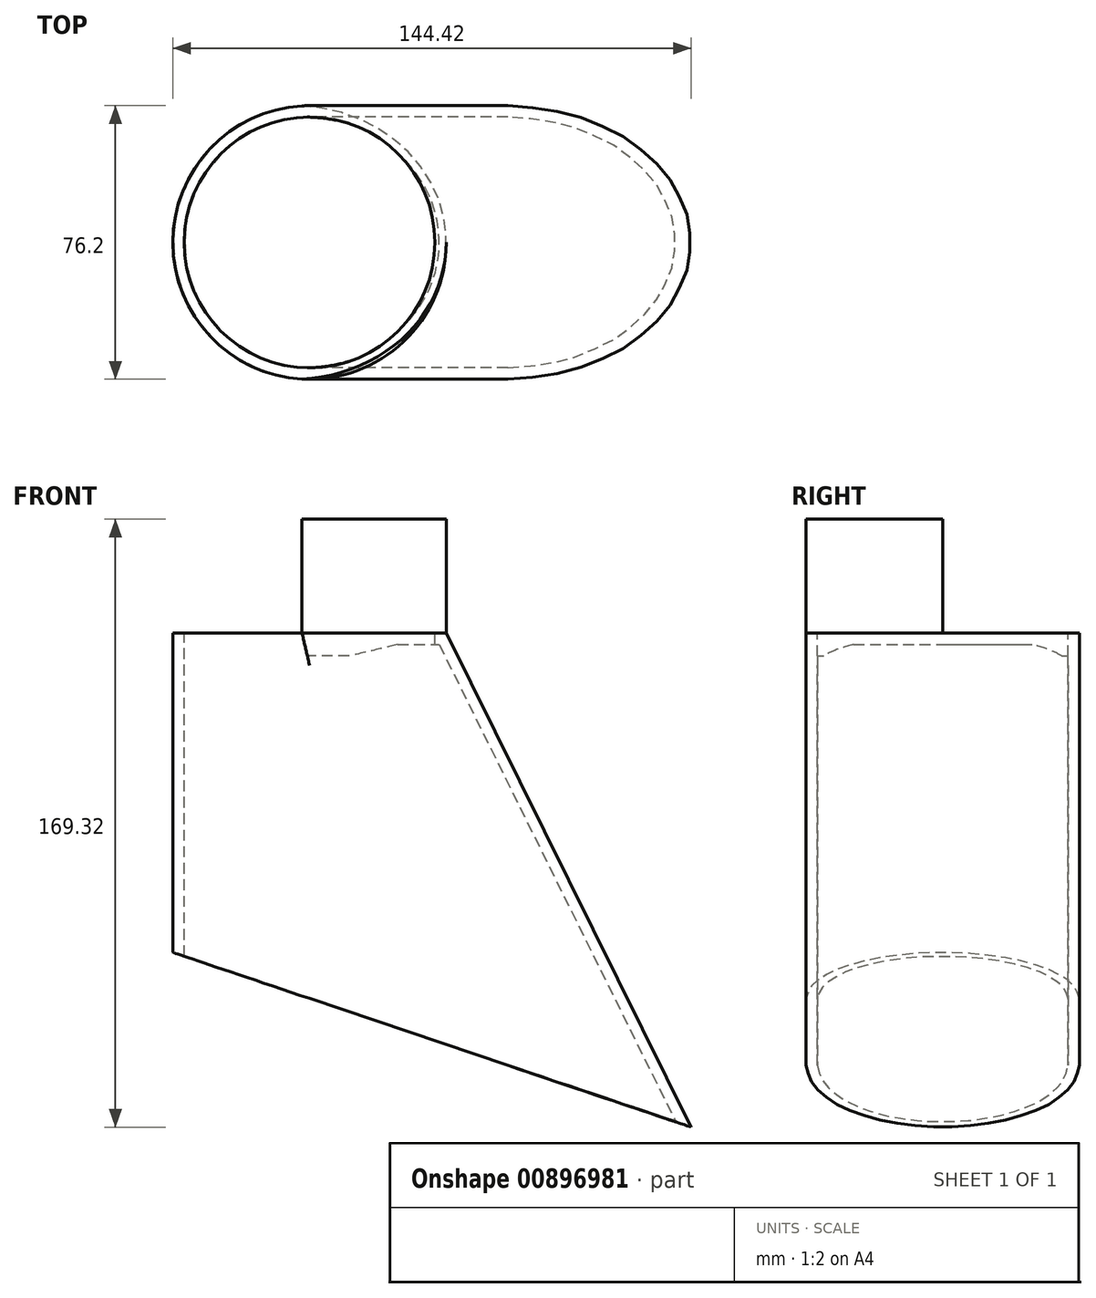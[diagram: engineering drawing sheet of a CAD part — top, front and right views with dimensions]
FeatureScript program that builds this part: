
annotation { "Feature Type Name" : "Feature", "Feature Type Description" : "" }
export const myFeature = defineFeature(function(context is Context, id is Id, definition is map)
    precondition{}
    {
        {
            var Q0;
            Q0=qCreatedBy(makeId("Front.planeOp"),FACE);
            var sketch = newSketch(context, id + "F0", { "sketchPlane" : qUnion([Q0])});
            skLineSegment(sketch, "E0", {"start": v(76.2, 88.9) * mm, "end": v(0, 88.9) * mm});
            skLineSegment(sketch, "E1", {"start": v(0, 88.9) * mm, "end": v(0, 0) * mm});
            skLineSegment(sketch, "E2", {"start": v(144.42, -48.67) * mm, "end": v(0, 0) * mm});
            skLineSegment(sketch, "E3", {"start": v(144.42, -48.67) * mm, "end": v(76.2, 88.9) * mm});
            skSolve(sketch);
        }
        {
            var Q0;
            Q0=makeQuery(id+"F0.imprint","IMPRINT",FACE,{"disambiguationData":[TD([[makeQuery(id+"F0.imprint","IMPRINT",EDGE,{"derivedFrom":sQuery(id+"F0.wireOp",EDGE,"E0")}),1.0]])]});
            extrude(context, id + "F1", {"entities" : qUnion([Q0]), "oppositeDirection" : true, "depth" : 76.2 * mm, "offsetDistance" : 25.4 * mm});
        }
        {
            var Q0;
            Q0=makeQuery(id+"F1.opExtrude","CAP_EDGE",EDGE,{"disambiguationData":[OSD([sQuery(id+"F0.wireOp",EDGE,"E1")])],"isStart":true});
            var Q1;
            Q1=makeQuery(id+"F1.opExtrude","CAP_EDGE",EDGE,{"disambiguationData":[OSD([sQuery(id+"F0.wireOp",EDGE,"E1")])],"isStart":false});
            var Q2;
            Q2=makeQuery(id+"F1.opExtrude","CAP_EDGE",EDGE,{"disambiguationData":[OSD([sQuery(id+"F0.wireOp",EDGE,"E3")])],"isStart":false});
            var Q3;
            Q3=makeQuery(id+"F1.opExtrude","CAP_EDGE",EDGE,{"disambiguationData":[OSD([sQuery(id+"F0.wireOp",EDGE,"E3")])],"isStart":true});
            fillet(context, id + "F2", {"entities" : qUnion([Q0, Q1, Q2, Q3]), "radius" : 38.1 * mm, "tangentPropagation" : true, "allowEdgeOverflow" : false});
        }
        {
            var Q0;
            Q0=makeQuery(id+"F1.opExtrude","SWEPT_FACE",FACE,{"disambiguationData":[OSD([sQuery(id+"F0.wireOp",EDGE,"E2")])]});
            shell(context, id + "F3", {"entities" : qUnion([Q0]), "thickness" : 3.17 * mm});
        }
        {
            var Q0;
            Q0=makeQuery(id+"F1.opExtrude","SWEPT_FACE",FACE,{"disambiguationData":[OSD([sQuery(id+"F0.wireOp",EDGE,"E0")])]});
            var sketch = newSketch(context, id + "F4", { "sketchPlane" : qUnion([Q0])});
            skCircle(sketch, "E4", {"center": v(38.1, 38.1) * mm, "radius": 38.1 * mm});
            skSolve(sketch);
        }
        {
            var Q0;
            {var subQ0=sQuery(id+"F4.wireOp",EDGE,"E4");var subQ1=makeQuery(id+"F2.opFillet","BLEND_EDGE",EDGE,{"blendedFrom":[makeQuery(id+"F1.opExtrude","CAP_EDGE",EDGE,{"disambiguationData":[OSD([sQuery(id+"F0.wireOp",EDGE,"E3")])],"isStart":true}),makeQuery(id+"F1.opExtrude","SWEPT_FACE",FACE,{"disambiguationData":[OSD([sQuery(id+"F0.wireOp",EDGE,"E0")])]})],"blendedInto":[makeQuery(id+"F1.opExtrude","SWEPT_FACE",FACE,{"disambiguationData":[OSD([sQuery(id+"F0.wireOp",EDGE,"E0")])]})]});var subQ2=makeQuery(id+"F4.imprint","INTERSECT",VERTEX,{"disambiguationData":[OD(0.0)],"derivedFrom":[subQ1,subQ0]});Q0=makeQuery(id+"F4.imprint","IMPRINT",FACE,{"disambiguationData":[TD([[makeQuery(id+"F4.imprint","IMPRINT",EDGE,{"disambiguationData":[TD([[subQ2,1.0]])],"derivedFrom":subQ0}),1.0]])]});}
            extrude(context, id + "F5", {"entities" : qUnion([Q0]), "operationType" : NewBodyOperationType.ADD, "depth" : 31.75 * mm, "offsetDistance" : 25.4 * mm});
        }
        {
            var Q0;
            Q0=makeQuery(id+"F5.opExtrude","CAP_FACE",FACE,{"disambiguationData":[OSD([sQuery(id+"F0.wireOp",EDGE,"E0"),sQuery(id+"F0.wireOp",EDGE,"E3"),sQuery(id+"F4.wireOp",EDGE,"E4")])],"isStart":false});
            var sketch = newSketch(context, id + "F6", { "sketchPlane" : qUnion([Q0])});
            skCircle(sketch, "E5", {"center": v(38.1, 38.1) * mm, "radius": 34.93 * mm});
            skSolve(sketch);
        }
        {
            var Q0;
            Q0=makeQuery(id+"F6.imprint","IMPRINT",FACE,{"disambiguationData":[TD([[makeQuery(id+"F6.imprint","IMPRINT",EDGE,{"derivedFrom":sQuery(id+"F6.wireOp",EDGE,"E5")}),1.0]])]});
            extrude(context, id + "F7", {"entities" : qUnion([Q0]), "operationType" : NewBodyOperationType.REMOVE, "oppositeDirection" : true, "depth" : 38.1 * mm, "offsetDistance" : 25.4 * mm});
        }
    });
